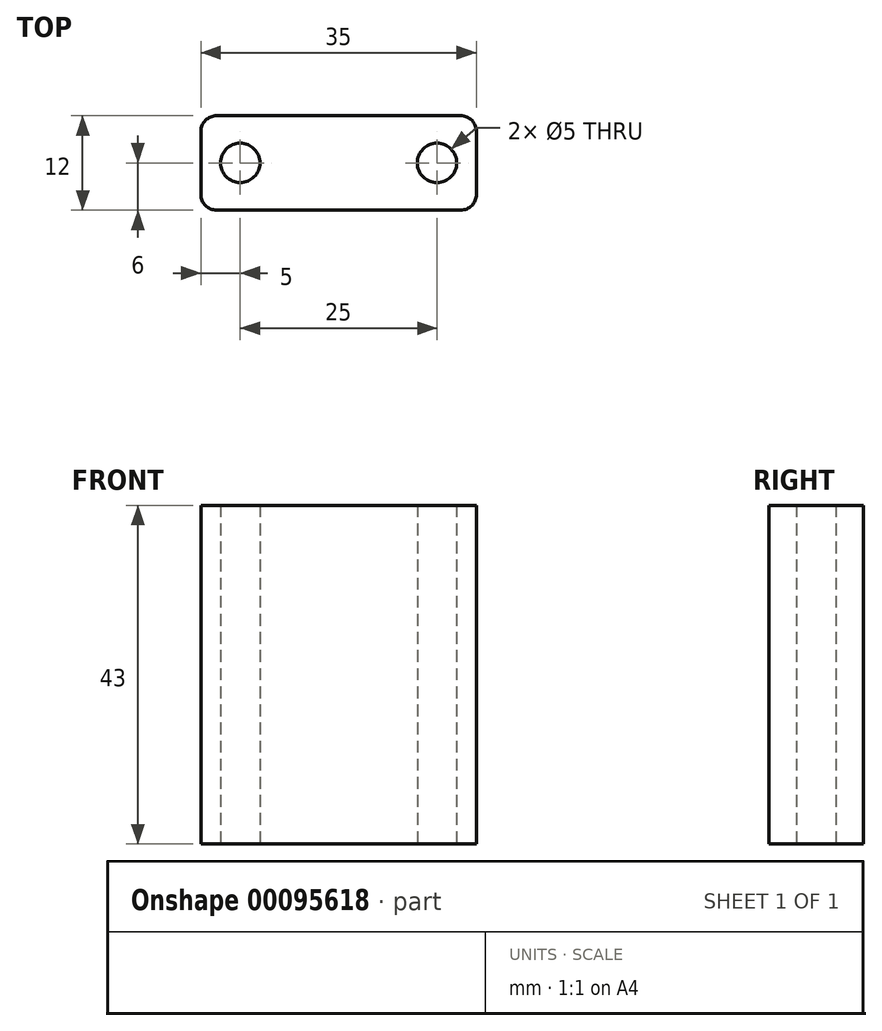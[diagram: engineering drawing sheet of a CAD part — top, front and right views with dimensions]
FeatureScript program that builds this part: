
annotation { "Feature Type Name" : "Feature", "Feature Type Description" : "" }
export const myFeature = defineFeature(function(context is Context, id is Id, definition is map)
    precondition{}
    {
        {
            var Q0;
            Q0=qCreatedBy(makeId("Top.planeOp"),FACE);
            var sketch = newSketch(context, id + "F0", { "sketchPlane" : qUnion([Q0])});
            skLineSegment(sketch, "E0.top", {"start": v(0, 6) * mm, "end": v(25, 6) * mm});
            skCircle(sketch, "E1", {"center": v(0, 0) * mm, "radius": 2.5 * mm});
            skCircle(sketch, "E2", {"center": v(25, 0) * mm, "radius": 2.5 * mm});
            skLineSegment(sketch, "E3.top", {"start": v(0, 6) * mm, "end": v(-5, 6) * mm});
            skLineSegment(sketch, "E3.right", {"start": v(-5, 0) * mm, "end": v(-5, 6) * mm});
            skLineSegment(sketch, "E4.top", {"start": v(25, 6) * mm, "end": v(30, 6) * mm});
            skLineSegment(sketch, "E4.right", {"start": v(30, 0) * mm, "end": v(30, 6) * mm});
            skLineSegment(sketch, "E5.MirrorCS", {"start": v(30, 0) * mm, "end": v(30, -6) * mm});
            skLineSegment(sketch, "E6.MirrorCS", {"start": v(25, -6) * mm, "end": v(30, -6) * mm});
            skLineSegment(sketch, "E7.MirrorCS", {"start": v(0, -6) * mm, "end": v(25, -6) * mm});
            skLineSegment(sketch, "E8.MirrorCS", {"start": v(-5, 0) * mm, "end": v(-5, -6) * mm});
            skLineSegment(sketch, "E9.MirrorCS", {"start": v(0, -6) * mm, "end": v(-5, -6) * mm});
            skSolve(sketch);
        }
        {
            var Q0;
            Q0=makeQuery(id+"F0.imprint","IMPRINT",FACE,{"disambiguationData":[TD([[makeQuery(id+"F0.imprint","IMPRINT",EDGE,{"derivedFrom":sQuery(id+"F0.wireOp",EDGE,"E0.top")}),-1.0]])]});
            extrude(context, id + "F1", {"entities" : qUnion([Q0]), "depth" : 43 * mm});
        }
        {
            var Q0;
            Q0=makeQuery(id+"F1.opExtrude","SWEPT_EDGE",EDGE,{"disambiguationData":[OSD([sQuery(id+"F0.wireOp",EDGE,"E8.MirrorCS"),sQuery(id+"F0.wireOp",EDGE,"E9.MirrorCS")])]});
            var Q1;
            Q1=makeQuery(id+"F1.opExtrude","SWEPT_EDGE",EDGE,{"disambiguationData":[OSD([sQuery(id+"F0.wireOp",EDGE,"E3.top"),sQuery(id+"F0.wireOp",EDGE,"E3.right")])]});
            var Q2;
            Q2=makeQuery(id+"F1.opExtrude","SWEPT_EDGE",EDGE,{"disambiguationData":[OSD([sQuery(id+"F0.wireOp",EDGE,"E5.MirrorCS"),sQuery(id+"F0.wireOp",EDGE,"E6.MirrorCS")])]});
            var Q3;
            Q3=makeQuery(id+"F1.opExtrude","SWEPT_EDGE",EDGE,{"disambiguationData":[OSD([sQuery(id+"F0.wireOp",EDGE,"E4.top"),sQuery(id+"F0.wireOp",EDGE,"E4.right")])]});
            fillet(context, id + "F2", {"entities" : qUnion([Q0, Q1, Q2, Q3]), "radius" : 2 * mm, "tangentPropagation" : true, "allowEdgeOverflow" : false});
        }
    });
